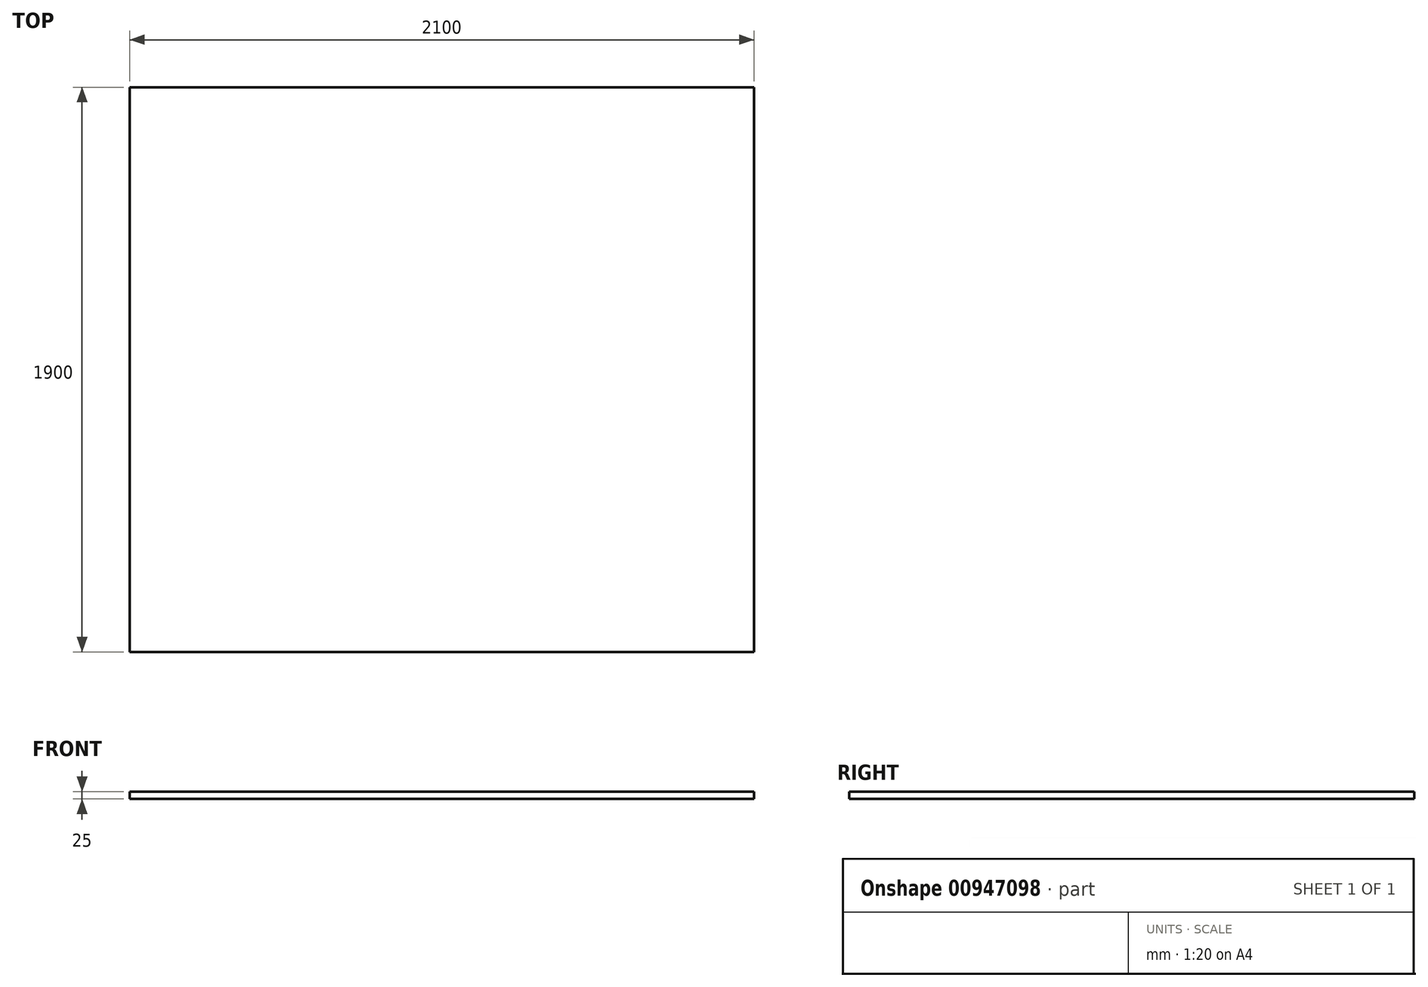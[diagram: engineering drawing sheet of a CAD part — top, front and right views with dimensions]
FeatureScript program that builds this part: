
annotation { "Feature Type Name" : "Feature", "Feature Type Description" : "" }
export const myFeature = defineFeature(function(context is Context, id is Id, definition is map)
    precondition{}
    {
        {
            var Q0;
            Q0=qCreatedBy(makeId("Top.planeOp"),FACE);
            var sketch = newSketch(context, id + "F0", { "sketchPlane" : qUnion([Q0])});
            skLineSegment(sketch, "E0.bottom", {"start": v(-1049.08, 993.18) * mm, "end": v(1050.92, 993.18) * mm});
            skLineSegment(sketch, "E0.top", {"start": v(-1049.08, -906.82) * mm, "end": v(1050.92, -906.82) * mm});
            skLineSegment(sketch, "E0.left", {"start": v(-1049.08, 993.18) * mm, "end": v(-1049.08, -906.82) * mm});
            skLineSegment(sketch, "E0.right", {"start": v(1050.92, 993.18) * mm, "end": v(1050.92, -906.82) * mm});
            skSolve(sketch);
        }
        {
            var Q0;
            Q0 = qSketchRegion(id + "F0", true);
            extrude(context, id + "F1", {"entities" : qUnion([Q0]), "depth" : 25 * mm, "offsetDistance" : 25 * mm});
        }
    });
